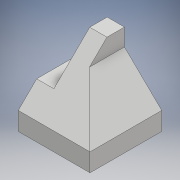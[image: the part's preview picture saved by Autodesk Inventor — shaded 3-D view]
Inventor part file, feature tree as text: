
AUTODESK INVENTOR PART (.ipt)
format: ipt  version: 2018 (Build 220112000, 112)  size: 121,344 bytes
history: native  units: mm
features: extrude x3, sketch x3
ambient origin geometry x8: Origin, YZ Plane, XZ Plane, XY Plane, X Axis, Y Axis, Z Axis, Center Point
bodies: Solid1 (feature_tree)
feature tree (6):
  extrude  "Extrusion1"  Depth=18.75mm
  extrude  "Extrusion2"  Depth=18.75mm
  extrude  "Extrusion3"  Depth=4.5mm
  sketch  "Sketch1"  dims[d0=18.75mm d1=18.75mm]
  sketch  "Sketch2"  dims[d2=18.75mm d3=0.0mm d4=4.75mm]
  sketch  "Sketch3"  dims[d5=4.5mm d6=7.9174mm d7=15.708057mm d8=21.0mm d9=0.0mm d10=4.5mm d11=9.25mm d12=4.5mm d13=4.5mm d14=4.75mm d15=27.25mm d16=0.0mm]
